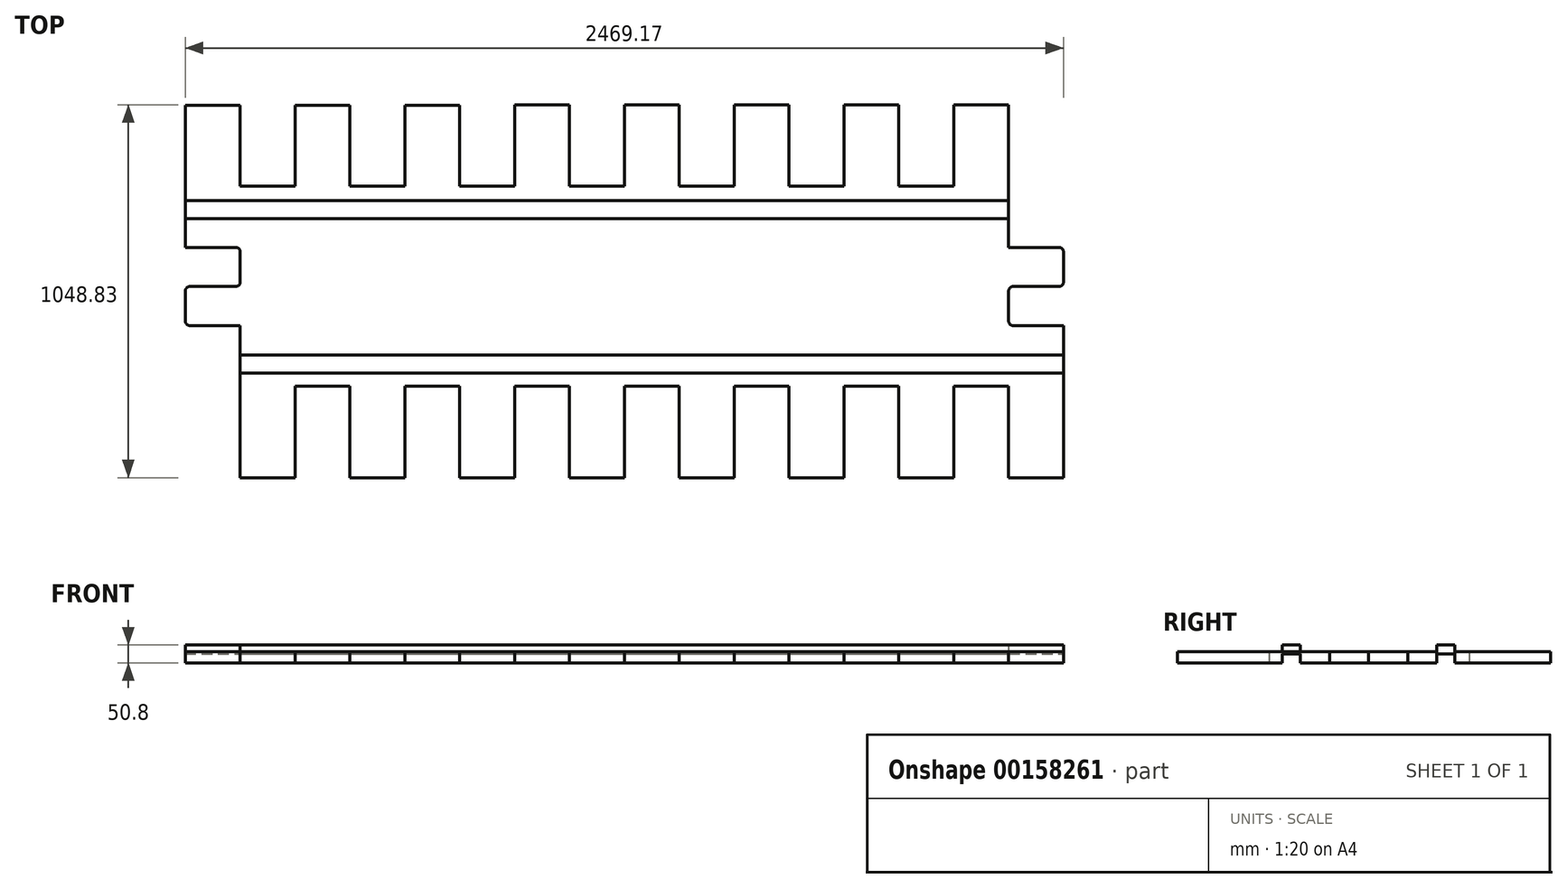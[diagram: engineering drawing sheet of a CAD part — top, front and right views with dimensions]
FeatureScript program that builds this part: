
annotation { "Feature Type Name" : "Feature", "Feature Type Description" : "" }
export const myFeature = defineFeature(function(context is Context, id is Id, definition is map)
    precondition{}
    {
        {
            var Q0;
            Q0=qCreatedBy(makeId("Top.planeOp"),FACE);
            var sketch = newSketch(context, id + "F0", { "sketchPlane" : qUnion([Q0])});
            skLineSegment(sketch, "E0", {"start": v(0, 0) * mm, "end": v(141.6, 0) * mm});
            skLineSegment(sketch, "E1", {"start": v(154.3, -12.7) * mm, "end": v(154.3, -97.3) * mm});
            skLineSegment(sketch, "E2", {"start": v(141.6, -110) * mm, "end": v(12.7, -110) * mm});
            skLineSegment(sketch, "E3", {"start": v(0, -122.7) * mm, "end": v(0, -207.32) * mm});
            skLineSegment(sketch, "E4", {"start": v(12.7, -220.02) * mm, "end": v(154.3, -220.02) * mm});
            skLineSegment(sketch, "E5", {"start": v(154.3, -220.02) * mm, "end": v(154.3, -647.87) * mm});
            skLineSegment(sketch, "E6", {"start": v(154.3, -647.87) * mm, "end": v(0, -647.87) * mm});
            skLineSegment(sketch, "E7", {"start": v(0, -647.87) * mm, "end": v(0, -389.82) * mm});
            skLineSegment(sketch, "E8", {"start": v(0, -389.82) * mm, "end": v(-154.3, -389.82) * mm});
            skLineSegment(sketch, "E9", {"start": v(-154.3, -389.82) * mm, "end": v(-154.3, -647.87) * mm});
            skLineSegment(sketch, "E10", {"start": v(-154.3, -647.87) * mm, "end": v(-308.61, -647.87) * mm});
            skLineSegment(sketch, "E11", {"start": v(-308.61, -647.87) * mm, "end": v(-308.61, -389.82) * mm});
            skLineSegment(sketch, "E12", {"start": v(-308.61, -389.82) * mm, "end": v(-462.92, -389.82) * mm});
            skLineSegment(sketch, "E13", {"start": v(-462.92, -389.82) * mm, "end": v(-462.92, -647.87) * mm});
            skLineSegment(sketch, "E14", {"start": v(-462.92, -647.87) * mm, "end": v(-617.22, -647.87) * mm});
            skLineSegment(sketch, "E15", {"start": v(-617.22, -647.87) * mm, "end": v(-617.22, -389.82) * mm});
            skLineSegment(sketch, "E16", {"start": v(-617.22, -389.82) * mm, "end": v(-771.53, -389.82) * mm});
            skLineSegment(sketch, "E17", {"start": v(-771.53, -389.82) * mm, "end": v(-771.53, -647.87) * mm});
            skLineSegment(sketch, "E18", {"start": v(-771.53, -647.87) * mm, "end": v(-925.83, -647.87) * mm});
            skLineSegment(sketch, "E19", {"start": v(-925.83, -647.87) * mm, "end": v(-925.83, -389.82) * mm});
            skPoint(sketch, "E20.visualSharp", {"position": v(154.3, 0) * mm});
            skArc(sketch, "E20.filletArc", {"start": v(154.3, -12.7) * mm, "mid": v(150.59, -3.72) * mm, "end": v(141.6, 0) * mm});
            skPoint(sketch, "E21.visualSharp", {"position": v(154.3, -110) * mm});
            skArc(sketch, "E21.filletArc", {"start": v(141.6, -110) * mm, "mid": v(150.59, -106.29) * mm, "end": v(154.3, -97.3) * mm});
            skPoint(sketch, "E22.visualSharp", {"position": v(0, -220.02) * mm});
            skArc(sketch, "E22.filletArc", {"start": v(0, -207.32) * mm, "mid": v(3.72, -216.3) * mm, "end": v(12.7, -220.02) * mm});
            skPoint(sketch, "E23.visualSharp", {"position": v(0, -110) * mm});
            skArc(sketch, "E23.filletArc", {"start": v(12.7, -110) * mm, "mid": v(3.72, -113.73) * mm, "end": v(0, -122.7) * mm});
            skLineSegment(sketch, "E24", {"start": v(-925.83, -389.82) * mm, "end": v(-1080.14, -389.82) * mm});
            skLineSegment(sketch, "E25", {"start": v(-1080.14, -389.82) * mm, "end": v(-1080.14, -647.87) * mm});
            skLineSegment(sketch, "E26", {"start": v(-1080.14, -647.87) * mm, "end": v(-1234.44, -647.87) * mm});
            skLineSegment(sketch, "E27", {"start": v(-1234.44, -647.87) * mm, "end": v(-1234.44, -389.82) * mm});
            skLineSegment(sketch, "E28", {"start": v(-1234.44, -389.82) * mm, "end": v(-1388.75, -389.82) * mm});
            skLineSegment(sketch, "E29", {"start": v(-1388.75, -389.82) * mm, "end": v(-1388.75, -647.87) * mm});
            skLineSegment(sketch, "E30", {"start": v(-1388.75, -647.87) * mm, "end": v(-1543.05, -647.87) * mm});
            skLineSegment(sketch, "E31", {"start": v(-1543.05, -647.87) * mm, "end": v(-1543.05, -389.82) * mm});
            skLineSegment(sketch, "E32", {"start": v(-1543.05, -389.82) * mm, "end": v(-1697.36, -389.82) * mm});
            skLineSegment(sketch, "E33", {"start": v(-1697.36, -389.82) * mm, "end": v(-1697.36, -647.87) * mm});
            skLineSegment(sketch, "E34", {"start": v(-1697.36, -647.87) * mm, "end": v(-1851.67, -647.87) * mm});
            skLineSegment(sketch, "E35", {"start": v(-1851.67, -647.87) * mm, "end": v(-1851.67, -389.82) * mm});
            skLineSegment(sketch, "E36", {"start": v(-1851.67, -389.82) * mm, "end": v(-2005.97, -389.82) * mm});
            skLineSegment(sketch, "E37", {"start": v(-2005.97, -389.82) * mm, "end": v(-2005.97, -647.87) * mm});
            skLineSegment(sketch, "E38", {"start": v(-2005.97, -647.87) * mm, "end": v(-2160.29, -647.87) * mm});
            skLineSegment(sketch, "E39", {"start": v(-2160.29, -647.87) * mm, "end": v(-2160.29, -220.02) * mm});
            skLineSegment(sketch, "E40", {"start": v(-2160.29, -220.02) * mm, "end": v(-2301.9, -220.02) * mm});
            skLineSegment(sketch, "E41", {"start": v(-2314.6, -207.32) * mm, "end": v(-2314.6, -122.7) * mm});
            skLineSegment(sketch, "E42", {"start": v(-2301.9, -110) * mm, "end": v(-2172.99, -110) * mm});
            skLineSegment(sketch, "E43", {"start": v(-2160.29, -97.3) * mm, "end": v(-2160.29, -12.7) * mm});
            skLineSegment(sketch, "E44", {"start": v(-2172.99, 0) * mm, "end": v(-2314.6, 0) * mm});
            skLineSegment(sketch, "E45", {"start": v(-2314.6, 0) * mm, "end": v(-2314.6, 399.88) * mm});
            skPoint(sketch, "E46.visualSharp", {"position": v(-2314.6, -110) * mm});
            skArc(sketch, "E46.filletArc", {"start": v(-2301.9, -110) * mm, "mid": v(-2310.87, -113.73) * mm, "end": v(-2314.6, -122.7) * mm});
            skPoint(sketch, "E47.visualSharp", {"position": v(-2314.6, -220.02) * mm});
            skArc(sketch, "E47.filletArc", {"start": v(-2314.6, -207.32) * mm, "mid": v(-2310.87, -216.3) * mm, "end": v(-2301.9, -220.02) * mm});
            skPoint(sketch, "E48.visualSharp", {"position": v(-2160.29, -110) * mm});
            skArc(sketch, "E48.filletArc", {"start": v(-2172.99, -110) * mm, "mid": v(-2164, -106.29) * mm, "end": v(-2160.29, -97.3) * mm});
            skPoint(sketch, "E49.visualSharp", {"position": v(-2160.29, 0) * mm});
            skArc(sketch, "E49.filletArc", {"start": v(-2160.29, -12.7) * mm, "mid": v(-2164, -3.72) * mm, "end": v(-2172.99, 0) * mm});
            skLineSegment(sketch, "E50", {"start": v(-2314.6, 399.88) * mm, "end": v(-2160.29, 399.88) * mm});
            skLineSegment(sketch, "E51", {"start": v(-2160.29, 399.88) * mm, "end": v(-2160.29, 172.14) * mm});
            skLineSegment(sketch, "E52", {"start": v(-2160.29, 172.14) * mm, "end": v(-2005.98, 172.14) * mm});
            skLineSegment(sketch, "E53", {"start": v(-2005.98, 172.14) * mm, "end": v(-2005.98, 399.88) * mm});
            skLineSegment(sketch, "E54", {"start": v(-2005.98, 399.88) * mm, "end": v(-1851.68, 399.88) * mm});
            skLineSegment(sketch, "E55", {"start": v(-1851.68, 399.88) * mm, "end": v(-1851.68, 172.14) * mm});
            skLineSegment(sketch, "E56", {"start": v(-1851.68, 172.14) * mm, "end": v(-1697.37, 172.14) * mm});
            skLineSegment(sketch, "E57", {"start": v(-1697.37, 172.14) * mm, "end": v(-1697.37, 399.88) * mm});
            skLineSegment(sketch, "E58", {"start": v(-1697.37, 399.88) * mm, "end": v(-1543.07, 399.88) * mm});
            skLineSegment(sketch, "E59", {"start": v(-1543.07, 399.88) * mm, "end": v(-1543.07, 172.14) * mm});
            skLineSegment(sketch, "E60", {"start": v(-1543.07, 172.14) * mm, "end": v(-1388.76, 172.14) * mm});
            skLineSegment(sketch, "E61", {"start": v(-1388.76, 172.14) * mm, "end": v(-1388.76, 400.96) * mm});
            skLineSegment(sketch, "E62", {"start": v(-1388.76, 400.96) * mm, "end": v(-1234.46, 400.96) * mm});
            skLineSegment(sketch, "E63", {"start": v(-1234.46, 400.96) * mm, "end": v(-1234.46, 172.14) * mm});
            skLineSegment(sketch, "E64", {"start": v(-1234.46, 172.14) * mm, "end": v(-1080.15, 172.14) * mm});
            skLineSegment(sketch, "E65", {"start": v(-1080.15, 172.14) * mm, "end": v(-1080.15, 400.96) * mm});
            skLineSegment(sketch, "E66", {"start": v(-1080.15, 400.96) * mm, "end": v(-925.85, 400.96) * mm});
            skLineSegment(sketch, "E67", {"start": v(-925.85, 400.96) * mm, "end": v(-925.85, 172.14) * mm});
            skLineSegment(sketch, "E68", {"start": v(-925.85, 172.14) * mm, "end": v(-771.54, 172.14) * mm});
            skLineSegment(sketch, "E69", {"start": v(-771.54, 172.14) * mm, "end": v(-771.54, 400.96) * mm});
            skLineSegment(sketch, "E70", {"start": v(-771.54, 400.96) * mm, "end": v(-617.24, 400.96) * mm});
            skLineSegment(sketch, "E71", {"start": v(-617.24, 400.96) * mm, "end": v(-617.24, 172.14) * mm});
            skLineSegment(sketch, "E72", {"start": v(-617.24, 172.14) * mm, "end": v(-462.93, 172.14) * mm});
            skLineSegment(sketch, "E73", {"start": v(-462.93, 172.14) * mm, "end": v(-462.93, 400.96) * mm});
            skLineSegment(sketch, "E74", {"start": v(-462.93, 400.96) * mm, "end": v(-308.63, 400.96) * mm});
            skLineSegment(sketch, "E75", {"start": v(-308.63, 400.96) * mm, "end": v(-308.63, 172.14) * mm});
            skLineSegment(sketch, "E76", {"start": v(-308.63, 172.14) * mm, "end": v(-154.32, 172.14) * mm});
            skLineSegment(sketch, "E77", {"start": v(-154.32, 172.14) * mm, "end": v(-154.32, 400.96) * mm});
            skLineSegment(sketch, "E78", {"start": v(-154.32, 400.96) * mm, "end": v(-0.02, 400.96) * mm});
            skLineSegment(sketch, "E79", {"start": v(-0.02, 400.96) * mm, "end": v(-0.02, 172.14) * mm});
            skLineSegment(sketch, "E80", {"start": v(-0.02, 172.14) * mm, "end": v(0, 0) * mm});
            skSolve(sketch);
        }
        {
            var Q0;
            Q0=makeQuery(id+"F0.imprint","IMPRINT",FACE,{"disambiguationData":[TD([[makeQuery(id+"F0.imprint","IMPRINT",EDGE,{"derivedFrom":sQuery(id+"F0.wireOp",EDGE,"E0")}),-1.0]])]});
            var sketch = newSketch(context, id + "F1", { "sketchPlane" : qUnion([Q0])});
            skLineSegment(sketch, "E81", {"start": v(-2314.86, 131.91) * mm, "end": v(0, 131.91) * mm});
            skLineSegment(sketch, "E82.0", {"start": v(-2314.86, 81.11) * mm, "end": v(0, 81.11) * mm});
            skLineSegment(sketch, "E83", {"start": v(-2160.59, -353.29) * mm, "end": v(154.12, -353.29) * mm});
            skLineSegment(sketch, "E84.0", {"start": v(-2160.59, -302.49) * mm, "end": v(154.12, -302.49) * mm});
            skLineSegment(sketch, "E85", {"start": v(-2314.86, 131.91) * mm, "end": v(-2314.86, 81.11) * mm});
            skLineSegment(sketch, "E86", {"start": v(-2160.59, -302.49) * mm, "end": v(-2160.59, -353.29) * mm});
            skLineSegment(sketch, "E87", {"start": v(154.12, -302.49) * mm, "end": v(154.12, -353.29) * mm});
            skLineSegment(sketch, "E88", {"start": v(0, 131.91) * mm, "end": v(0, 81.11) * mm});
            skSolve(sketch);
        }
        {
            var Q0;
            Q0=qSketchRegion(id+"F0",true);
            extrude(context, id + "F2", {"entities" : qUnion([Q0]), "depth" : 31.75 * mm});
        }
        {
            var Q0;
            Q0=qSketchRegion(id+"F1",true);
            extrude(context, id + "F3", {"entities" : qUnion([Q0]), "operationType" : NewBodyOperationType.ADD, "depth" : 50.8 * mm});
        }
        {
            var Q0;
            Q0=makeQuery(id+"F3.boolean.opBoolean","MERGE",FACE,{"derivedFrom":[makeQuery(id+"F2.opExtrude","CAP_FACE",FACE,{"disambiguationData":[OSD([sQuery(id+"F0.wireOp",EDGE,"E0"),sQuery(id+"F0.wireOp",EDGE,"E1"),sQuery(id+"F0.wireOp",EDGE,"E2"),sQuery(id+"F0.wireOp",EDGE,"E3"),sQuery(id+"F0.wireOp",EDGE,"E4"),sQuery(id+"F0.wireOp",EDGE,"E5"),sQuery(id+"F0.wireOp",EDGE,"E6"),sQuery(id+"F0.wireOp",EDGE,"E7"),sQuery(id+"F0.wireOp",EDGE,"E8"),sQuery(id+"F0.wireOp",EDGE,"E9"),sQuery(id+"F0.wireOp",EDGE,"E10"),sQuery(id+"F0.wireOp",EDGE,"E11"),sQuery(id+"F0.wireOp",EDGE,"E12"),sQuery(id+"F0.wireOp",EDGE,"E13"),sQuery(id+"F0.wireOp",EDGE,"E14"),sQuery(id+"F0.wireOp",EDGE,"E15"),sQuery(id+"F0.wireOp",EDGE,"E16"),sQuery(id+"F0.wireOp",EDGE,"E17"),sQuery(id+"F0.wireOp",EDGE,"E18"),sQuery(id+"F0.wireOp",EDGE,"E19"),sQuery(id+"F0.wireOp",EDGE,"E20.filletArc"),sQuery(id+"F0.wireOp",EDGE,"E21.filletArc"),sQuery(id+"F0.wireOp",EDGE,"E22.filletArc"),sQuery(id+"F0.wireOp",EDGE,"E23.filletArc"),sQuery(id+"F0.wireOp",EDGE,"E24"),sQuery(id+"F0.wireOp",EDGE,"E25"),sQuery(id+"F0.wireOp",EDGE,"E26"),sQuery(id+"F0.wireOp",EDGE,"E27"),sQuery(id+"F0.wireOp",EDGE,"E28"),sQuery(id+"F0.wireOp",EDGE,"E29"),sQuery(id+"F0.wireOp",EDGE,"E30"),sQuery(id+"F0.wireOp",EDGE,"E31"),sQuery(id+"F0.wireOp",EDGE,"E32"),sQuery(id+"F0.wireOp",EDGE,"E33"),sQuery(id+"F0.wireOp",EDGE,"E34"),sQuery(id+"F0.wireOp",EDGE,"E35"),sQuery(id+"F0.wireOp",EDGE,"E36"),sQuery(id+"F0.wireOp",EDGE,"E37"),sQuery(id+"F0.wireOp",EDGE,"E38"),sQuery(id+"F0.wireOp",EDGE,"E39"),sQuery(id+"F0.wireOp",EDGE,"E40"),sQuery(id+"F0.wireOp",EDGE,"E41"),sQuery(id+"F0.wireOp",EDGE,"E42"),sQuery(id+"F0.wireOp",EDGE,"E43"),sQuery(id+"F0.wireOp",EDGE,"E44"),sQuery(id+"F0.wireOp",EDGE,"E45"),sQuery(id+"F0.wireOp",EDGE,"E46.filletArc"),sQuery(id+"F0.wireOp",EDGE,"E47.filletArc"),sQuery(id+"F0.wireOp",EDGE,"E48.filletArc"),sQuery(id+"F0.wireOp",EDGE,"E49.filletArc"),sQuery(id+"F0.wireOp",EDGE,"E50"),sQuery(id+"F0.wireOp",EDGE,"E51"),sQuery(id+"F0.wireOp",EDGE,"E52"),sQuery(id+"F0.wireOp",EDGE,"E53"),sQuery(id+"F0.wireOp",EDGE,"E54"),sQuery(id+"F0.wireOp",EDGE,"E55"),sQuery(id+"F0.wireOp",EDGE,"E56"),sQuery(id+"F0.wireOp",EDGE,"E57"),sQuery(id+"F0.wireOp",EDGE,"E58"),sQuery(id+"F0.wireOp",EDGE,"E59"),sQuery(id+"F0.wireOp",EDGE,"E60"),sQuery(id+"F0.wireOp",EDGE,"E61"),sQuery(id+"F0.wireOp",EDGE,"E62"),sQuery(id+"F0.wireOp",EDGE,"E63"),sQuery(id+"F0.wireOp",EDGE,"E64"),sQuery(id+"F0.wireOp",EDGE,"E65"),sQuery(id+"F0.wireOp",EDGE,"E66"),sQuery(id+"F0.wireOp",EDGE,"E67"),sQuery(id+"F0.wireOp",EDGE,"E68"),sQuery(id+"F0.wireOp",EDGE,"E69"),sQuery(id+"F0.wireOp",EDGE,"E70"),sQuery(id+"F0.wireOp",EDGE,"E71"),sQuery(id+"F0.wireOp",EDGE,"E72"),sQuery(id+"F0.wireOp",EDGE,"E73"),sQuery(id+"F0.wireOp",EDGE,"E74"),sQuery(id+"F0.wireOp",EDGE,"E75"),sQuery(id+"F0.wireOp",EDGE,"E76"),sQuery(id+"F0.wireOp",EDGE,"E77"),sQuery(id+"F0.wireOp",EDGE,"E78"),sQuery(id+"F0.wireOp",EDGE,"E79"),sQuery(id+"F0.wireOp",EDGE,"E80")])],"isStart":true}),makeQuery(id+"F3.opExtrude","CAP_FACE",FACE,{"disambiguationData":[OSD([sQuery(id+"F1.wireOp",EDGE,"E81"),sQuery(id+"F1.wireOp",EDGE,"E82.0"),sQuery(id+"F1.wireOp",EDGE,"E85"),sQuery(id+"F1.wireOp",EDGE,"E88")])],"isStart":true}),makeQuery(id+"F3.opExtrude","CAP_FACE",FACE,{"disambiguationData":[OSD([sQuery(id+"F1.wireOp",EDGE,"E83"),sQuery(id+"F1.wireOp",EDGE,"E84.0"),sQuery(id+"F1.wireOp",EDGE,"E86"),sQuery(id+"F1.wireOp",EDGE,"E87")])],"isStart":true})]});
            var sketch = newSketch(context, id + "F4", { "sketchPlane" : qUnion([Q0])});
            skLineSegment(sketch, "E89", {"start": v(-2314.6, -131.91) * mm, "end": v(0, -131.91) * mm});
            skLineSegment(sketch, "E90", {"start": v(0, -81.11) * mm, "end": v(-2314.6, -81.11) * mm});
            skLineSegment(sketch, "E91", {"start": v(-2160.29, 302.49) * mm, "end": v(154.3, 302.49) * mm});
            skLineSegment(sketch, "E92", {"start": v(-2160.29, 353.29) * mm, "end": v(154.3, 353.29) * mm});
            skSolve(sketch);
        }
        {
            var Q0;
            {var subQ6=sQuery(id+"F1.wireOp",EDGE,"E85");Q0=makeQuery(id+"F4.imprint","IMPRINT",FACE,{"disambiguationData":[TD([[makeQuery(id+"F4.imprint","IMPRINT",EDGE,{"derivedFrom":makeQuery(id+"F3.opExtrude","CAP_EDGE",EDGE,{"disambiguationData":[OSD([subQ6])],"isStart":true})}),-1.0]])]});}
            var Q1;
            {var subQ1=sQuery(id+"F4.wireOp",EDGE,"E91");Q1=makeQuery(id+"F4.imprint","IMPRINT",FACE,{"disambiguationData":[TD([[makeQuery(id+"F4.imprint","IMPRINT",EDGE,{"derivedFrom":subQ1}),1.0]])]});}
            extrude(context, id + "F5", {"entities" : qUnion([Q0, Q1]), "operationType" : NewBodyOperationType.REMOVE, "oppositeDirection" : true, "depth" : 25.4 * mm});
        }
    });
